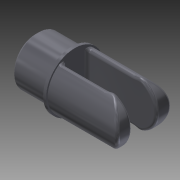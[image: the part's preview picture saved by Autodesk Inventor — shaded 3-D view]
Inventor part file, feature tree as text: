
AUTODESK INVENTOR PART (.ipt)
format: ipt  version: 2011 SP2 (Build 150309200, 309)  size: 324,096 bytes
history: native  units: mm
features: fillet x3, sketch x3, extrude x2, revolve x1, chamfer x1
ambient origin geometry x8: Origin, YZ Plane, XZ Plane, XY Plane, X Axis, Y Axis, Z Axis, Center Point
bodies: Solid1 (feature_tree)
feature tree (10):
  revolve  "Revolution1"  [1 undecoded]
  extrude  "Extrusion1"  Depth=1.0mm
  chamfer  "Chamfer1"  Distance=23.0mm
  fillet  "Fillet1"  [1 undecoded]
  fillet  "Fillet2"  Radius=4.0mm
  extrude  "Extrusion2"  Depth=4.0mm
  fillet  "Fillet3"  Radius=100.0mm
  sketch  "Sketch1"  dims[d0=12.0mm d1=8.0mm]
  sketch  "Sketch2"  dims[d2=1.5mm d3=1.0mm]
  sketch  "Sketch3"  dims[d4=0.5mm d5=23.0mm d7=90.0deg d10=4.0mm d11=4.0mm d12=100.0mm d13=0.0mm d14=1.0mm d15=2.0mm d16=45.0deg d17=1.0mm d18=1.0mm d19=16.124515mm d20=8.0mm d21=8.0mm d22=100.0mm d23=0.0mm d24=1.0mm]
note: 2 required parameter values undecoded (feature->parameter linkage not recoverable at this tier; creation-order binding heuristic only, values carry confidence <= 0.55)